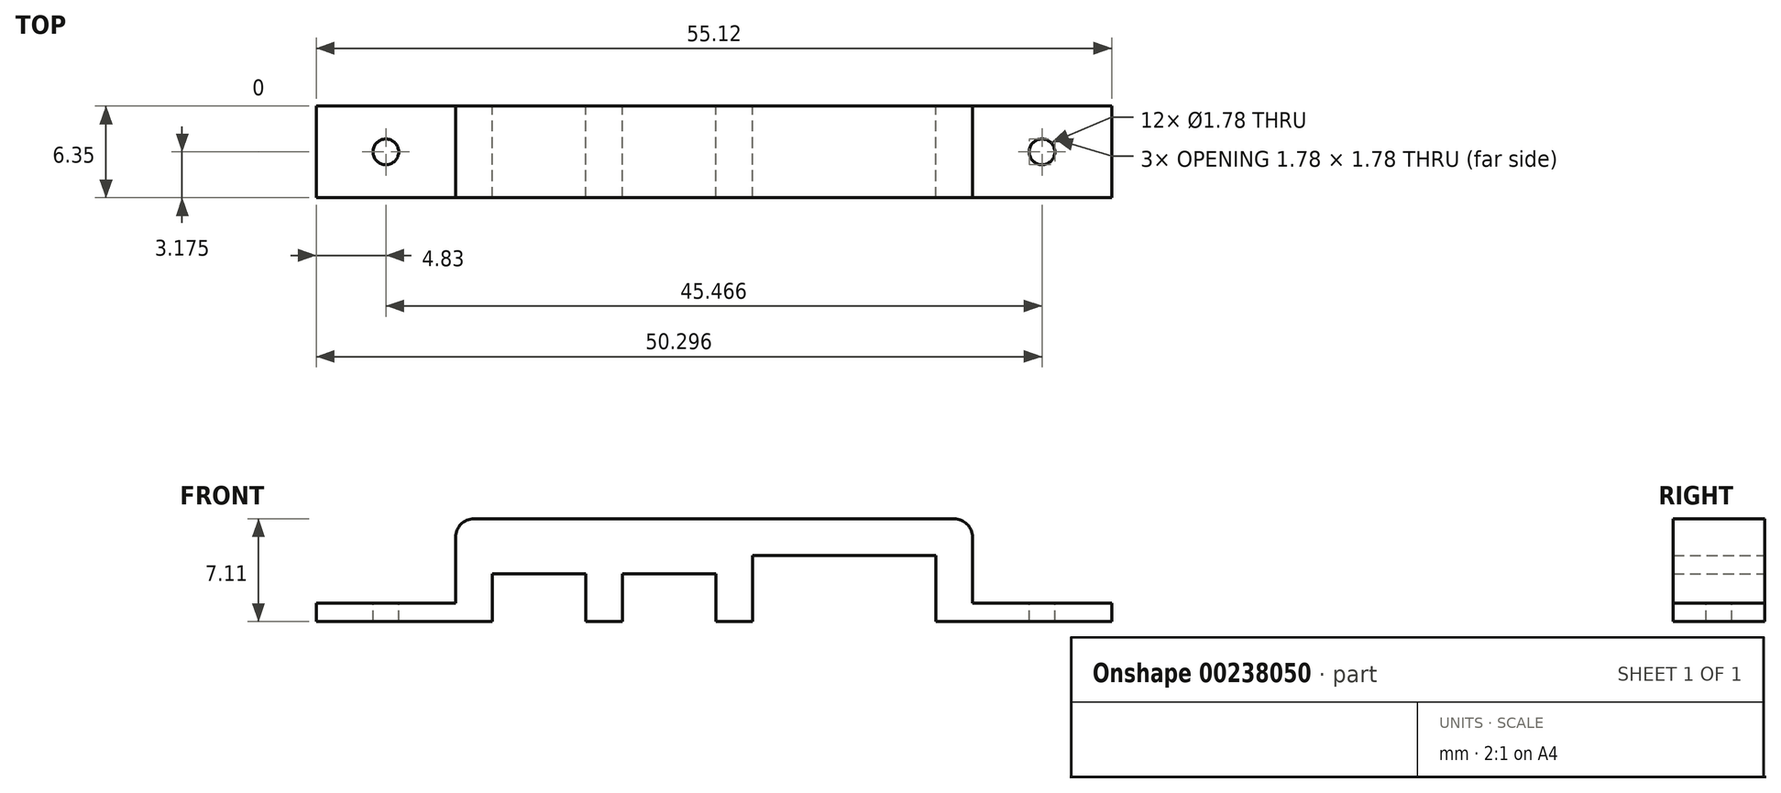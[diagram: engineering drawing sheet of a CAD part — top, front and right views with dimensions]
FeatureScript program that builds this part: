
annotation { "Feature Type Name" : "Feature", "Feature Type Description" : "" }
export const myFeature = defineFeature(function(context is Context, id is Id, definition is map)
    precondition{}
    {
        {
            var Q0;
            Q0=qCreatedBy(makeId("Front.planeOp"),FACE);
            var sketch = newSketch(context, id + "F0", { "sketchPlane" : qUnion([Q0])});
            skLineSegment(sketch, "E0", {"start": v(15.28, 0) * mm, "end": v(15.28, 4.57) * mm});
            skLineSegment(sketch, "E1", {"start": v(15.28, 4.57) * mm, "end": v(2.58, 4.57) * mm});
            skLineSegment(sketch, "E2", {"start": v(2.58, 4.57) * mm, "end": v(2.58, 0) * mm});
            skLineSegment(sketch, "E3", {"start": v(2.58, 0) * mm, "end": v(0.04, 0) * mm});
            skLineSegment(sketch, "E4", {"start": v(0.04, 0) * mm, "end": v(0.04, 3.3) * mm});
            skLineSegment(sketch, "E5", {"start": v(0.04, 3.3) * mm, "end": v(-6.44, 3.3) * mm});
            skLineSegment(sketch, "E6", {"start": v(-6.44, 3.3) * mm, "end": v(-6.44, 0) * mm});
            skLineSegment(sketch, "E7", {"start": v(-6.44, 0) * mm, "end": v(-8.98, 0) * mm});
            skLineSegment(sketch, "E8", {"start": v(-8.98, 0) * mm, "end": v(-8.98, 3.3) * mm});
            skLineSegment(sketch, "E9", {"start": v(-8.98, 3.3) * mm, "end": v(-15.45, 3.3) * mm});
            skLineSegment(sketch, "E10", {"start": v(-15.45, 3.3) * mm, "end": v(-15.45, 0) * mm});
            skLineSegment(sketch, "E11", {"start": v(-15.45, 0) * mm, "end": v(-18, 0) * mm});
            skLineSegment(sketch, "E12", {"start": v(-18, 1.27) * mm, "end": v(-18, 5.84) * mm});
            skLineSegment(sketch, "E13", {"start": v(-16.72, 7.11) * mm, "end": v(16.55, 7.11) * mm});
            skLineSegment(sketch, "E14", {"start": v(17.82, 5.84) * mm, "end": v(17.82, 1.27) * mm});
            skLineSegment(sketch, "E15", {"start": v(17.82, 0) * mm, "end": v(15.28, 0) * mm});
            skPoint(sketch, "E16.visualSharp", {"position": v(-18, 7.11) * mm});
            skArc(sketch, "E16.filletArc", {"start": v(-16.72, 7.11) * mm, "mid": v(-17.62, 6.74) * mm, "end": v(-18, 5.84) * mm});
            skPoint(sketch, "E17.visualSharp", {"position": v(17.82, 7.11) * mm});
            skArc(sketch, "E17.filletArc", {"start": v(17.82, 5.84) * mm, "mid": v(17.45, 6.74) * mm, "end": v(16.55, 7.11) * mm});
            skLineSegment(sketch, "E18", {"start": v(-18, 1.27) * mm, "end": v(-27.65, 1.27) * mm});
            skLineSegment(sketch, "E19", {"start": v(-27.65, 1.27) * mm, "end": v(-27.65, 0) * mm});
            skLineSegment(sketch, "E20", {"start": v(-27.65, 0) * mm, "end": v(-18, 0) * mm});
            skLineSegment(sketch, "E21", {"start": v(17.82, 1.27) * mm, "end": v(27.47, 1.27) * mm});
            skLineSegment(sketch, "E22", {"start": v(27.47, 1.27) * mm, "end": v(27.47, 0) * mm});
            skLineSegment(sketch, "E23", {"start": v(27.47, 0) * mm, "end": v(17.82, 0) * mm});
            skSolve(sketch);
        }
        {
            var Q0;
            Q0=makeQuery(id+"F0.imprint","IMPRINT",FACE,{"disambiguationData":[TD([[makeQuery(id+"F0.imprint","IMPRINT",EDGE,{"derivedFrom":sQuery(id+"F0.wireOp",EDGE,"E0")}),-1.0]])]});
            extrude(context, id + "F1", {"entities" : qUnion([Q0]), "depth" : 6.35 * mm});
        }
        {
            var Q0;
            Q0=makeQuery(id+"F1.opExtrude","SWEPT_FACE",FACE,{"disambiguationData":[OSD([sQuery(id+"F0.wireOp",EDGE,"E18")])]});
            var sketch = newSketch(context, id + "F2", { "sketchPlane" : qUnion([Q0])});
            skCircle(sketch, "E24", {"center": v(-22.82, -3.18) * mm, "radius": 0.89 * mm});
            skPoint(sketch, "E24.centerSnap0", {"position": v(-22.82, 0) * mm});
            skCircle(sketch, "E25", {"center": v(22.65, -3.18) * mm, "radius": 0.89 * mm});
            skSolve(sketch);
        }
        {
            var Q0;
            Q0=makeQuery(id+"F2.imprint","IMPRINT",FACE,{"disambiguationData":[TD([[makeQuery(id+"F2.imprint","IMPRINT",EDGE,{"derivedFrom":sQuery(id+"F2.wireOp",EDGE,"E24")}),1.0]])]});
            var Q1;
            Q1=makeQuery(id+"F2.imprint","IMPRINT",FACE,{"disambiguationData":[TD([[makeQuery(id+"F2.imprint","IMPRINT",EDGE,{"derivedFrom":sQuery(id+"F2.wireOp",EDGE,"E25")}),1.0]])]});
            extrude(context, id + "F3", {"entities" : qUnion([Q0, Q1]), "operationType" : NewBodyOperationType.REMOVE, "endBound" : BoundingType.UP_TO_NEXT, "oppositeDirection" : true, "depth" : 25.4 * mm});
        }
    });
